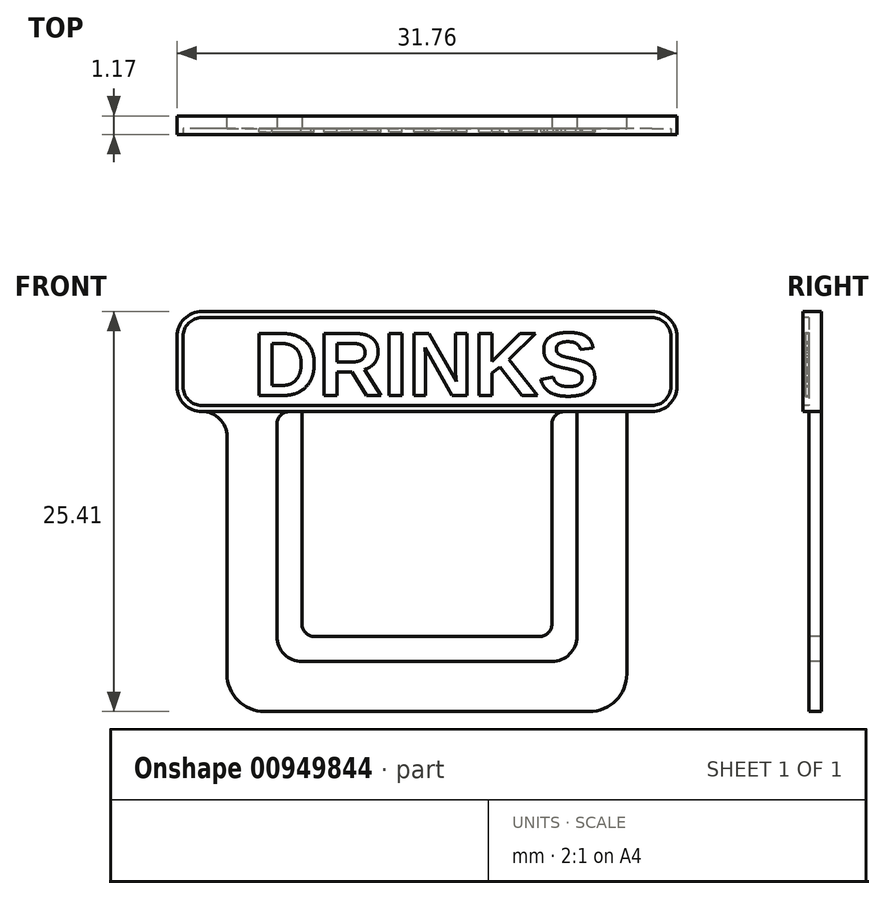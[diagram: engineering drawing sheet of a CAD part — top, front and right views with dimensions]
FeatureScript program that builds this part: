
annotation { "Feature Type Name" : "Feature", "Feature Type Description" : "" }
export const myFeature = defineFeature(function(context is Context, id is Id, definition is map)
    precondition{}
    {
        {
            var Q0;
            Q0=qCreatedBy(makeId("Front.planeOp"),FACE);
            var sketch = newSketch(context, id + "F0", { "sketchPlane" : qUnion([Q0])});
            skLineSegment(sketch, "E0.bottom", {"start": v(12.7, 9.53) * mm, "end": v(-12.7, 9.53) * mm});
            skLineSegment(sketch, "E0.top", {"start": v(12.7, -9.53) * mm, "end": v(-12.7, -9.53) * mm});
            skLineSegment(sketch, "E0.left", {"start": v(12.7, 9.53) * mm, "end": v(12.7, -9.53) * mm});
            skLineSegment(sketch, "E0.right", {"start": v(-12.7, 9.53) * mm, "end": v(-12.7, -9.53) * mm});
            skPoint(sketch, "E0.middle", {"position": v(0, 0) * mm});
            skSolve(sketch);
        }
        {
            var Q0;
            Q0=makeQuery(id+"F0.imprint","IMPRINT",FACE,{"disambiguationData":[TD([[makeQuery(id+"F0.imprint","IMPRINT",EDGE,{"derivedFrom":sQuery(id+"F0.wireOp",EDGE,"E0.bottom")}),1.0]])]});
            extrude(context, id + "F1", {"entities" : qUnion([Q0]), "depth" : 0.8 * mm, "offsetDistance" : 25.4 * mm});
        }
        {
            var Q0;
            Q0=makeQuery(id+"F1.opExtrude","SWEPT_EDGE",EDGE,{"disambiguationData":[OSD([sQuery(id+"F0.wireOp",EDGE,"E0.top"),sQuery(id+"F0.wireOp",EDGE,"E0.left")])]});
            var Q1;
            Q1=makeQuery(id+"F1.opExtrude","SWEPT_EDGE",EDGE,{"disambiguationData":[OSD([sQuery(id+"F0.wireOp",EDGE,"E0.top"),sQuery(id+"F0.wireOp",EDGE,"E0.right")])]});
            fillet(context, id + "F2", {"entities" : qUnion([Q0, Q1]), "radius" : 2.38 * mm, "tangentPropagation" : true, "allowEdgeOverflow" : false});
        }
        {
            var Q0;
            Q0=makeQuery(id+"F1.opExtrude","CAP_FACE",FACE,{"disambiguationData":[OSD([sQuery(id+"F0.wireOp",EDGE,"E0.bottom"),sQuery(id+"F0.wireOp",EDGE,"E0.top"),sQuery(id+"F0.wireOp",EDGE,"E0.left"),sQuery(id+"F0.wireOp",EDGE,"E0.right")])],"isStart":false});
            var sketch = newSketch(context, id + "F3", { "sketchPlane" : qUnion([Q0])});
            skLineSegment(sketch, "E1.bottom", {"start": v(9.52, 9.53) * mm, "end": v(-9.53, 9.53) * mm});
            skLineSegment(sketch, "E1.top", {"start": v(9.53, -6.35) * mm, "end": v(-9.53, -6.35) * mm});
            skLineSegment(sketch, "E1.left", {"start": v(9.52, 9.53) * mm, "end": v(9.53, -6.35) * mm});
            skLineSegment(sketch, "E1.right", {"start": v(-9.53, 9.53) * mm, "end": v(-9.52, -6.35) * mm});
            skPoint(sketch, "E1.middle", {"position": v(0, 0) * mm});
            skSolve(sketch);
        }
        {
            var Q0;
            Q0=makeQuery(id+"F3.imprint","IMPRINT",FACE,{"disambiguationData":[TD([[makeQuery(id+"F3.imprint","IMPRINT",EDGE,{"derivedFrom":sQuery(id+"F3.wireOp",EDGE,"E1.bottom")}),1.0]])]});
            extrude(context, id + "F4", {"entities" : qUnion([Q0]), "operationType" : NewBodyOperationType.REMOVE, "oppositeDirection" : true, "depth" : 4.93 * mm, "offsetDistance" : 25.4 * mm});
        }
        {
            var Q0;
            Q0=makeQuery(id+"F1.opExtrude","CAP_FACE",FACE,{"disambiguationData":[OSD([sQuery(id+"F0.wireOp",EDGE,"E0.bottom"),sQuery(id+"F0.wireOp",EDGE,"E0.top"),sQuery(id+"F0.wireOp",EDGE,"E0.left"),sQuery(id+"F0.wireOp",EDGE,"E0.right")])],"isStart":false});
            var sketch = newSketch(context, id + "F5", { "sketchPlane" : qUnion([Q0])});
            skLineSegment(sketch, "E2.bottom", {"start": v(-15.88, 9.53) * mm, "end": v(15.87, 9.53) * mm});
            skLineSegment(sketch, "E2.top", {"start": v(-15.88, 15.88) * mm, "end": v(15.87, 15.88) * mm});
            skLineSegment(sketch, "E2.left", {"start": v(-15.88, 9.53) * mm, "end": v(-15.88, 15.88) * mm});
            skLineSegment(sketch, "E2.right", {"start": v(15.87, 9.53) * mm, "end": v(15.87, 15.88) * mm});
            skSolve(sketch);
        }
        {
            var Q0;
            Q0=makeQuery(id+"F5.imprint","IMPRINT",FACE,{"disambiguationData":[TD([[makeQuery(id+"F5.imprint","IMPRINT",EDGE,{"derivedFrom":sQuery(id+"F5.wireOp",EDGE,"E2.top")}),-1.0]])]});
            extrude(context, id + "F6", {"entities" : qUnion([Q0]), "operationType" : NewBodyOperationType.ADD, "oppositeDirection" : true, "depth" : 0.8 * mm, "offsetDistance" : 25.4 * mm});
        }
        {
            var Q0;
            Q0=makeQuery(id+"F6.opExtrude","SWEPT_EDGE",EDGE,{"disambiguationData":[OSD([sQuery(id+"F5.wireOp",EDGE,"E2.top"),sQuery(id+"F5.wireOp",EDGE,"E2.left")])]});
            var Q1;
            Q1=makeQuery(id+"F6.opExtrude","SWEPT_EDGE",EDGE,{"disambiguationData":[OSD([sQuery(id+"F5.wireOp",EDGE,"E2.top"),sQuery(id+"F5.wireOp",EDGE,"E2.right")])]});
            var Q2;
            Q2=makeQuery(id+"F6.opExtrude","SWEPT_EDGE",EDGE,{"disambiguationData":[OSD([sQuery(id+"F5.wireOp",EDGE,"E2.bottom"),sQuery(id+"F5.wireOp",EDGE,"E2.right")])]});
            var Q3;
            Q3=makeQuery(id+"F1.opExtrude","SWEPT_EDGE",EDGE,{"disambiguationData":[OSD([sQuery(id+"F0.wireOp",EDGE,"E0.bottom"),sQuery(id+"F0.wireOp",EDGE,"E0.left")])]});
            var Q4;
            Q4=makeQuery(id+"F6.opExtrude","SWEPT_EDGE",EDGE,{"disambiguationData":[OSD([sQuery(id+"F5.wireOp",EDGE,"E2.bottom"),sQuery(id+"F5.wireOp",EDGE,"E2.left")])]});
            var Q5;
            Q5=makeQuery(id+"F1.opExtrude","SWEPT_EDGE",EDGE,{"disambiguationData":[OSD([sQuery(id+"F0.wireOp",EDGE,"E0.bottom"),sQuery(id+"F0.wireOp",EDGE,"E0.right")])]});
            fillet(context, id + "F7", {"entities" : qUnion([Q0, Q1, Q2, Q3, Q4, Q5]), "radius" : 1.59 * mm, "tangentPropagation" : true, "allowEdgeOverflow" : false});
        }
        {
            var Q0;
            Q0=makeQuery(id+"F4.boolean.opBoolean","COPY",EDGE,{"derivedFrom":makeQuery(id+"F4.opExtrude","SWEPT_EDGE",EDGE,{"disambiguationData":[OSD([sQuery(id+"F3.wireOp",EDGE,"E1.top"),sQuery(id+"F3.wireOp",EDGE,"E1.right")])]})});
            var Q1;
            Q1=makeQuery(id+"F4.boolean.opBoolean","COPY",EDGE,{"derivedFrom":makeQuery(id+"F4.opExtrude","SWEPT_EDGE",EDGE,{"disambiguationData":[OSD([sQuery(id+"F3.wireOp",EDGE,"E1.top"),sQuery(id+"F3.wireOp",EDGE,"E1.left")])]})});
            fillet(context, id + "F8", {"entities" : qUnion([Q0, Q1]), "radius" : 1.59 * mm, "tangentPropagation" : true, "allowEdgeOverflow" : false});
        }
        {
            var Q0;
            Q0=makeQuery(id+"F6.boolean.opBoolean","MERGE",FACE,{"derivedFrom":[makeQuery(id+"F1.opExtrude","CAP_FACE",FACE,{"disambiguationData":[OSD([sQuery(id+"F0.wireOp",EDGE,"E0.bottom"),sQuery(id+"F0.wireOp",EDGE,"E0.top"),sQuery(id+"F0.wireOp",EDGE,"E0.left"),sQuery(id+"F0.wireOp",EDGE,"E0.right")])],"isStart":false}),makeQuery(id+"F6.opExtrude","CAP_FACE",FACE,{"disambiguationData":[OSD([sQuery(id+"F5.wireOp",EDGE,"E2.bottom"),sQuery(id+"F5.wireOp",EDGE,"E2.top"),sQuery(id+"F5.wireOp",EDGE,"E2.left"),sQuery(id+"F5.wireOp",EDGE,"E2.right")])],"isStart":true})]});
            var sketch = newSketch(context, id + "F9", { "sketchPlane" : qUnion([Q0])});
            skLineSegment(sketch, "E3.bottom", {"start": v(-7.94, 9.53) * mm, "end": v(7.94, 9.53) * mm});
            skLineSegment(sketch, "E3.top", {"start": v(-7.94, -4.76) * mm, "end": v(7.94, -4.76) * mm});
            skLineSegment(sketch, "E3.left", {"start": v(-7.94, 9.53) * mm, "end": v(-7.94, -4.76) * mm});
            skLineSegment(sketch, "E3.right", {"start": v(7.94, 9.53) * mm, "end": v(7.94, -4.76) * mm});
            skSolve(sketch);
        }
        {
            var Q0;
            Q0=makeQuery(id+"F9.imprint","IMPRINT",FACE,{"disambiguationData":[TD([[makeQuery(id+"F9.imprint","IMPRINT",EDGE,{"derivedFrom":sQuery(id+"F9.wireOp",EDGE,"E3.bottom")}),1.0]])]});
            extrude(context, id + "F10", {"entities" : qUnion([Q0]), "operationType" : NewBodyOperationType.ADD, "oppositeDirection" : true, "depth" : 0.8 * mm, "offsetDistance" : 25.4 * mm});
        }
        {
            var Q0;
            Q0=makeQuery(id+"F10.opExtrude","SWEPT_EDGE",EDGE,{"disambiguationData":[OSD([sQuery(id+"F5.wireOp",EDGE,"E2.bottom"),sQuery(id+"F9.wireOp",EDGE,"E3.bottom"),sQuery(id+"F9.wireOp",EDGE,"E3.left")])]});
            var Q1;
            Q1=makeQuery(id+"F4.boolean.opBoolean","COPY",EDGE,{"derivedFrom":makeQuery(id+"F4.opExtrude","SWEPT_EDGE",EDGE,{"disambiguationData":[OSD([sQuery(id+"F0.wireOp",EDGE,"E0.bottom"),sQuery(id+"F3.wireOp",EDGE,"E1.bottom"),sQuery(id+"F3.wireOp",EDGE,"E1.right")])]})});
            var Q2;
            Q2=makeQuery(id+"F10.opExtrude","SWEPT_EDGE",EDGE,{"disambiguationData":[OSD([sQuery(id+"F5.wireOp",EDGE,"E2.bottom"),sQuery(id+"F9.wireOp",EDGE,"E3.bottom"),sQuery(id+"F9.wireOp",EDGE,"E3.right")])]});
            var Q3;
            Q3=makeQuery(id+"F4.boolean.opBoolean","COPY",EDGE,{"derivedFrom":makeQuery(id+"F4.opExtrude","SWEPT_EDGE",EDGE,{"disambiguationData":[OSD([sQuery(id+"F0.wireOp",EDGE,"E0.bottom"),sQuery(id+"F3.wireOp",EDGE,"E1.bottom"),sQuery(id+"F3.wireOp",EDGE,"E1.left")])]})});
            fillet(context, id + "F11", {"entities" : qUnion([Q0, Q1, Q2, Q3]), "radius" : 0.8 * mm, "tangentPropagation" : true, "allowEdgeOverflow" : false});
        }
        {
            var Q0;
            Q0=makeQuery(id+"F10.opExtrude","SWEPT_EDGE",EDGE,{"disambiguationData":[OSD([sQuery(id+"F9.wireOp",EDGE,"E3.top"),sQuery(id+"F9.wireOp",EDGE,"E3.left")])]});
            var Q1;
            Q1=makeQuery(id+"F10.opExtrude","SWEPT_EDGE",EDGE,{"disambiguationData":[OSD([sQuery(id+"F9.wireOp",EDGE,"E3.top"),sQuery(id+"F9.wireOp",EDGE,"E3.right")])]});
            fillet(context, id + "F12", {"entities" : qUnion([Q0, Q1]), "radius" : 0.8 * mm, "tangentPropagation" : true, "allowEdgeOverflow" : false});
        }
        {
            var Q0;
            Q0=makeQuery(id+"F10.boolean.opBoolean","MERGE",FACE,{"derivedFrom":[makeQuery(id+"F6.boolean.opBoolean","MERGE",FACE,{"derivedFrom":[makeQuery(id+"F1.opExtrude","CAP_FACE",FACE,{"disambiguationData":[OSD([sQuery(id+"F0.wireOp",EDGE,"E0.bottom"),sQuery(id+"F0.wireOp",EDGE,"E0.top"),sQuery(id+"F0.wireOp",EDGE,"E0.left"),sQuery(id+"F0.wireOp",EDGE,"E0.right")])],"isStart":false}),makeQuery(id+"F6.opExtrude","CAP_FACE",FACE,{"disambiguationData":[OSD([sQuery(id+"F5.wireOp",EDGE,"E2.bottom"),sQuery(id+"F5.wireOp",EDGE,"E2.top"),sQuery(id+"F5.wireOp",EDGE,"E2.left"),sQuery(id+"F5.wireOp",EDGE,"E2.right")])],"isStart":true})]}),makeQuery(id+"F10.opExtrude","CAP_FACE",FACE,{"disambiguationData":[OSD([sQuery(id+"F9.wireOp",EDGE,"E3.bottom"),sQuery(id+"F9.wireOp",EDGE,"E3.top"),sQuery(id+"F9.wireOp",EDGE,"E3.left"),sQuery(id+"F9.wireOp",EDGE,"E3.right")])],"isStart":true})]});
            var sketch = newSketch(context, id + "F13", { "sketchPlane" : qUnion([Q0])});
            skArc(sketch, "E4.0", {"start": v(-14.29, 15.88) * mm, "mid": v(-15.41, 15.41) * mm, "end": v(-15.88, 14.29) * mm});
            skLineSegment(sketch, "E5.0", {"start": v(-15.88, 11.11) * mm, "end": v(-15.88, 14.29) * mm});
            skArc(sketch, "E6.0", {"start": v(-15.88, 11.11) * mm, "mid": v(-15.41, 9.99) * mm, "end": v(-14.29, 9.53) * mm});
            skLineSegment(sketch, "E7.0", {"start": v(-14.29, 15.88) * mm, "end": v(14.29, 15.88) * mm});
            skArc(sketch, "E8.0", {"start": v(15.87, 14.29) * mm, "mid": v(15.41, 15.41) * mm, "end": v(14.29, 15.88) * mm});
            skLineSegment(sketch, "E9.0", {"start": v(15.87, 11.11) * mm, "end": v(15.87, 14.29) * mm});
            skArc(sketch, "E10.0", {"start": v(14.29, 9.53) * mm, "mid": v(15.41, 9.99) * mm, "end": v(15.87, 11.11) * mm});
            skLineSegment(sketch, "E11", {"start": v(-14.29, 9.53) * mm, "end": v(14.29, 9.53) * mm});
            skSolve(sketch);
        }
        {
            var Q0;
            Q0=makeQuery(id+"F13.imprint","IMPRINT",FACE,{"disambiguationData":[TD([[makeQuery(id+"F13.imprint","IMPRINT",EDGE,{"derivedFrom":sQuery(id+"F13.wireOp",EDGE,"E4.0")}),1.0]])]});
            extrude(context, id + "F14", {"entities" : qUnion([Q0]), "operationType" : NewBodyOperationType.ADD, "depth" : 0.38 * mm, "offsetDistance" : 25.4 * mm});
        }
        {
            var Q0;
            Q0=makeQuery(id+"F14.opExtrude","CAP_FACE",FACE,{"disambiguationData":[OSD([sQuery(id+"F13.wireOp",EDGE,"E4.0"),sQuery(id+"F13.wireOp",EDGE,"E5.0"),sQuery(id+"F13.wireOp",EDGE,"E6.0"),sQuery(id+"F13.wireOp",EDGE,"E7.0"),sQuery(id+"F13.wireOp",EDGE,"E8.0"),sQuery(id+"F13.wireOp",EDGE,"E9.0"),sQuery(id+"F13.wireOp",EDGE,"E10.0"),sQuery(id+"F13.wireOp",EDGE,"E11")])],"isStart":false});
            var sketch = newSketch(context, id + "F15", { "sketchPlane" : qUnion([Q0])});
            skArc(sketch, "E12.0", {"start": v(-14.29, 15.88) * mm, "mid": v(-15.41, 15.41) * mm, "end": v(-15.88, 14.29) * mm});
            skLineSegment(sketch, "E13.0", {"start": v(-14.29, 15.88) * mm, "end": v(14.29, 15.88) * mm});
            skLineSegment(sketch, "E14.0", {"start": v(-15.88, 11.11) * mm, "end": v(-15.88, 14.29) * mm});
            skArc(sketch, "E15.0", {"start": v(-15.88, 11.11) * mm, "mid": v(-15.41, 9.99) * mm, "end": v(-14.29, 9.53) * mm});
            skLineSegment(sketch, "E16.0", {"start": v(-14.29, 9.53) * mm, "end": v(14.29, 9.53) * mm});
            skArc(sketch, "E17.0", {"start": v(14.29, 9.53) * mm, "mid": v(15.41, 9.99) * mm, "end": v(15.87, 11.11) * mm});
            skArc(sketch, "E18.0", {"start": v(15.87, 14.29) * mm, "mid": v(15.41, 15.41) * mm, "end": v(14.29, 15.88) * mm});
            skArc(sketch, "E19", {"start": v(-14.29, 15.5) * mm, "mid": v(-15.14, 15.14) * mm, "end": v(-15.5, 14.29) * mm});
            skArc(sketch, "E20", {"start": v(-15.5, 11.11) * mm, "mid": v(-15.14, 10.26) * mm, "end": v(-14.29, 9.9) * mm});
            skArc(sketch, "E21", {"start": v(15.5, 14.29) * mm, "mid": v(15.14, 15.14) * mm, "end": v(14.29, 15.5) * mm});
            skArc(sketch, "E22", {"start": v(14.29, 9.9) * mm, "mid": v(15.14, 10.26) * mm, "end": v(15.5, 11.11) * mm});
            skLineSegment(sketch, "E23", {"start": v(-14.29, 15.88) * mm, "end": v(-14.29, 9.53) * mm, "construction": true});
            skLineSegment(sketch, "E24", {"start": v(-15.87, 14.29) * mm, "end": v(15.87, 14.29) * mm, "construction": true});
            skLineSegment(sketch, "E25", {"start": v(14.29, 15.88) * mm, "end": v(14.29, 9.53) * mm, "construction": true});
            skLineSegment(sketch, "E26", {"start": v(15.88, 11.11) * mm, "end": v(-15.88, 11.11) * mm, "construction": true});
            skLineSegment(sketch, "E27", {"start": v(14.29, 15.5) * mm, "end": v(-14.29, 15.5) * mm});
            skLineSegment(sketch, "E28", {"start": v(-15.5, 14.29) * mm, "end": v(-15.5, 11.11) * mm});
            skLineSegment(sketch, "E29", {"start": v(-14.29, 9.9) * mm, "end": v(14.29, 9.9) * mm});
            skLineSegment(sketch, "E30", {"start": v(15.5, 14.29) * mm, "end": v(15.5, 11.11) * mm});
            skSolve(sketch);
        }
        {
            var Q0;
            Q0=makeQuery(id+"F15.imprint","IMPRINT",FACE,{"disambiguationData":[TD([[makeQuery(id+"F15.imprint","IMPRINT",EDGE,{"derivedFrom":sQuery(id+"F15.wireOp",EDGE,"E19")}),1.0]])]});
            var Q1;
            {var subQ0=sQuery(id+"F9.wireOp",EDGE,"E3.right");var subQ1=sQuery(id+"F9.wireOp",EDGE,"E3.top");var subQ3=sQuery(id+"F0.wireOp",EDGE,"E0.bottom");var subQ4=sQuery(id+"F9.wireOp",EDGE,"E3.left");var subQ5=makeQuery(id+"F6.opExtrude","CAP_FACE",FACE,{"disambiguationData":[OSD([sQuery(id+"F5.wireOp",EDGE,"E2.bottom"),sQuery(id+"F5.wireOp",EDGE,"E2.top"),sQuery(id+"F5.wireOp",EDGE,"E2.left"),sQuery(id+"F5.wireOp",EDGE,"E2.right")])],"isStart":true});var subQ6=makeQuery(id+"F1.opExtrude","CAP_FACE",FACE,{"disambiguationData":[OSD([subQ3,sQuery(id+"F0.wireOp",EDGE,"E0.top"),sQuery(id+"F0.wireOp",EDGE,"E0.left"),sQuery(id+"F0.wireOp",EDGE,"E0.right")])],"isStart":false});var subQ7=makeQuery(id+"F10.opExtrude","CAP_FACE",FACE,{"disambiguationData":[OSD([sQuery(id+"F9.wireOp",EDGE,"E3.bottom"),subQ1,subQ4,subQ0])],"isStart":true});Q1=makeQuery(id+"F14.boolean.opBoolean","SPLIT",FACE,{"disambiguationData":[TD([makeQuery(id+"F10.opExtrude","SWEPT_FACE",FACE,{"disambiguationData":[OSD([subQ1])]})])],"derivedFrom":makeQuery(id+"F10.boolean.opBoolean","MERGE",FACE,{"derivedFrom":[makeQuery(id+"F6.boolean.opBoolean","MERGE",FACE,{"derivedFrom":[subQ6,subQ5]}),subQ7]})});}
            extrude(context, id + "F16", {"entities" : qUnion([Q0]), "operationType" : NewBodyOperationType.REMOVE, "endBound" : BoundingType.UP_TO_SURFACE, "oppositeDirection" : true, "depth" : 25.4 * mm, "endBoundEntityFace" : qUnion([Q1]), "offsetDistance" : 25.4 * mm});
        }
        {
            var Q0;
            Q0=qCreatedBy(makeId("Front.planeOp"),FACE);
            var sketch = newSketch(context, id + "F17", { "sketchPlane" : qUnion([Q0])});
            skText(sketch, "E31", { "text": "DRINKS", "fontName": "Arimo-Bold.ttf"});
            const initialGuessF17  = {"E31": [-0.01105, 0.01055, 1, 0, 0.00412]};
            skSetInitialGuess(sketch, initialGuessF17);
            skSolve(sketch);
        }
        {
            var Q0;
            Q0=qSketchRegion(id+"F17",true);
            extrude(context, id + "F18", {"entities" : qUnion([Q0]), "operationType" : NewBodyOperationType.ADD, "depth" : 1.02 * mm, "offsetDistance" : 25.4 * mm});
        }
    });
